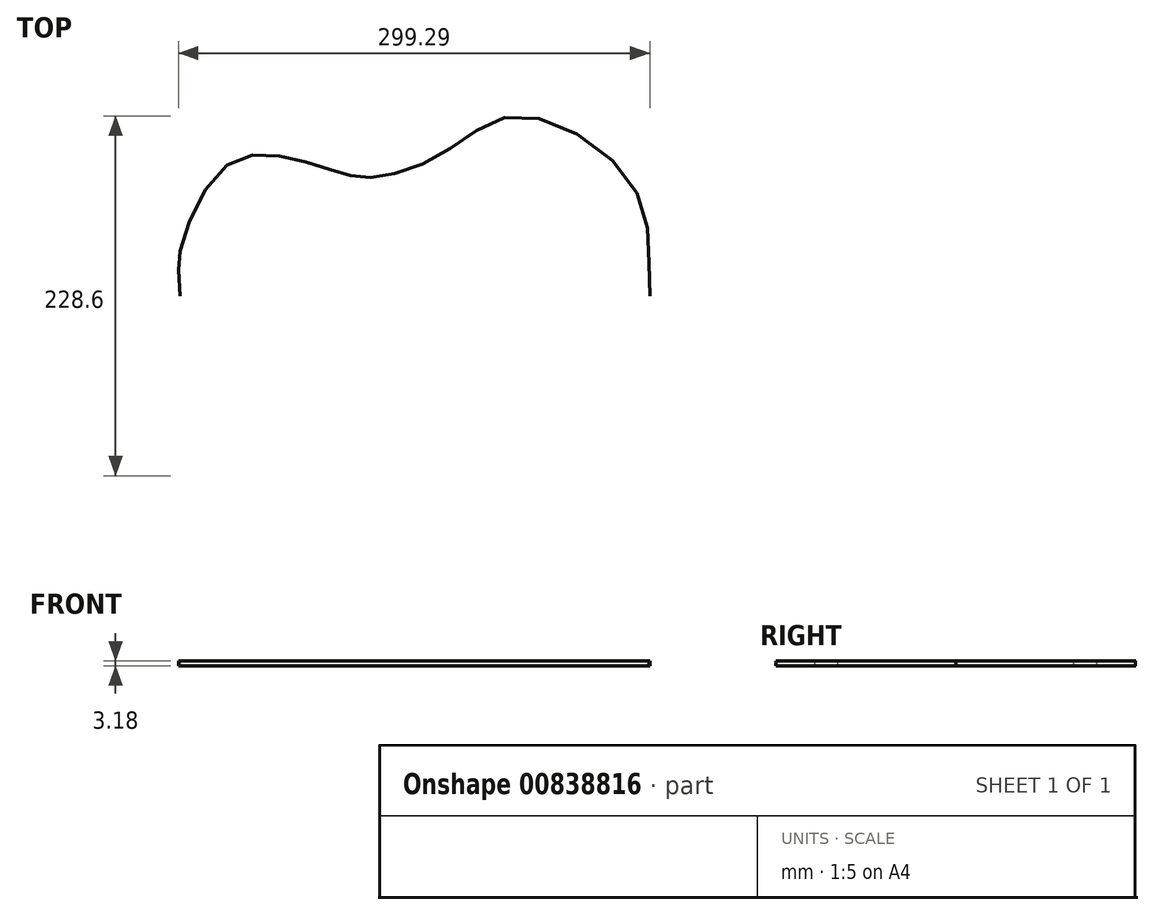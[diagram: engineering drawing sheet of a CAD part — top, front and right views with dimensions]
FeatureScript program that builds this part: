
annotation { "Feature Type Name" : "Feature", "Feature Type Description" : "" }
export const myFeature = defineFeature(function(context is Context, id is Id, definition is map)
    precondition{}
    {
        {
            var Q0;
            Q0=qCreatedBy(makeId("Top.planeOp"),FACE);
            var sketch = newSketch(context, id + "F0", { "sketchPlane" : qUnion([Q0])});
            skFitSpline(sketch, "E0", {"points": [v(-123.83, 0) * mm, v(-123.83, -28.13) * mm, v(-96, -81.4) * mm, v(-57.15, -88.27) * mm, v(-22.78, -78.36) * mm, v(0, -75.4) * mm, v(42.93, -90.56) * mm, v(92.08, -114.3) * mm, v(166.2, -65.98) * mm, v(174.63, 0) * mm], "startDerivative": vector(0, -540.72) * mm, "endDerivative": vector(49.2, 458.31) * mm});
            skFitSpline(sketch, "E1.MirrorCS", {"points": [v(-123.83, 0) * mm, v(-123.83, 28.13) * mm, v(-96, 81.4) * mm, v(-57.15, 88.27) * mm, v(-22.78, 78.36) * mm, v(0, 75.4) * mm, v(42.93, 90.56) * mm, v(92.08, 114.3) * mm, v(166.2, 65.98) * mm, v(174.63, 0) * mm], "startDerivative": vector(0, 540.72) * mm, "endDerivative": vector(49.2, -458.31) * mm});
            skSolve(sketch);
        }
        {
            var Q0;
            Q0=qSketchRegion(id+"F0",true);
            extrude(context, id + "F1", {"entities" : qUnion([Q0]), "depth" : 3.17 * mm, "offsetDistance" : 25.4 * mm});
        }
    });
